# Revit family: ARKOSLIGHT_Track 3L
name_source: partatom
category: Lighting Fixtures
units: mm (PartAtom-declared; Revit-internal decimal feet)

## family parameters
Cut with Voids When Loaded = No
Host = Face
Light Source = No
Part Type = Normal
Room Calculation Point = No
Round Connector Dimension = Use Diameter
Shared = No

## types (4) — shared parameters
ARKOSLIGHT_Fixture Type = ACCESSORIES
ARKOSLIGHT_Model = ACCESSORIES
Apparent Load = 0 VA
Description = Select the number and length of profiles suitable for the defined length
Manufacturer = ARKOSLIGHT
Model = ACCESSORIES
URL = https://www.arkoslight.com
zero-valued in all types: Default Elevation

## per-type parameters (varying)
| type | ARKOSLIGHT_Body Color | ARKOSLIGHT_Color | ARKOSLIGHT_Dimming | ARKOSLIGHT_Reference | ARKOSLIGHT_Series |
| A2820X00B - TRACK 3L XM B | ARKOSLIGHT_White | White | No | A2820X00B | ACCESORIOS TRACK 3L |
| A2820X00N - TRACK 3L XM N | ARKOSLIGHT_Black | Black | No | A2820X00N | ACCESORIOS TRACK 3L |
| A219210XB - TRACK 3L DIM DALI XM B | ARKOSLIGHT_White | White | Yes | A219210XB | ACCESORIOS TRACK 3L DIM |
| A219210XN - TRACK 3L DIM DALI XM N | ARKOSLIGHT_Black | Black | Yes | A219210XN | ACCESORIOS TRACK 3L DIM |

## geometry (parser evidence)
native form markers: Sweep x2
no freeform markers — native parametric forms only
